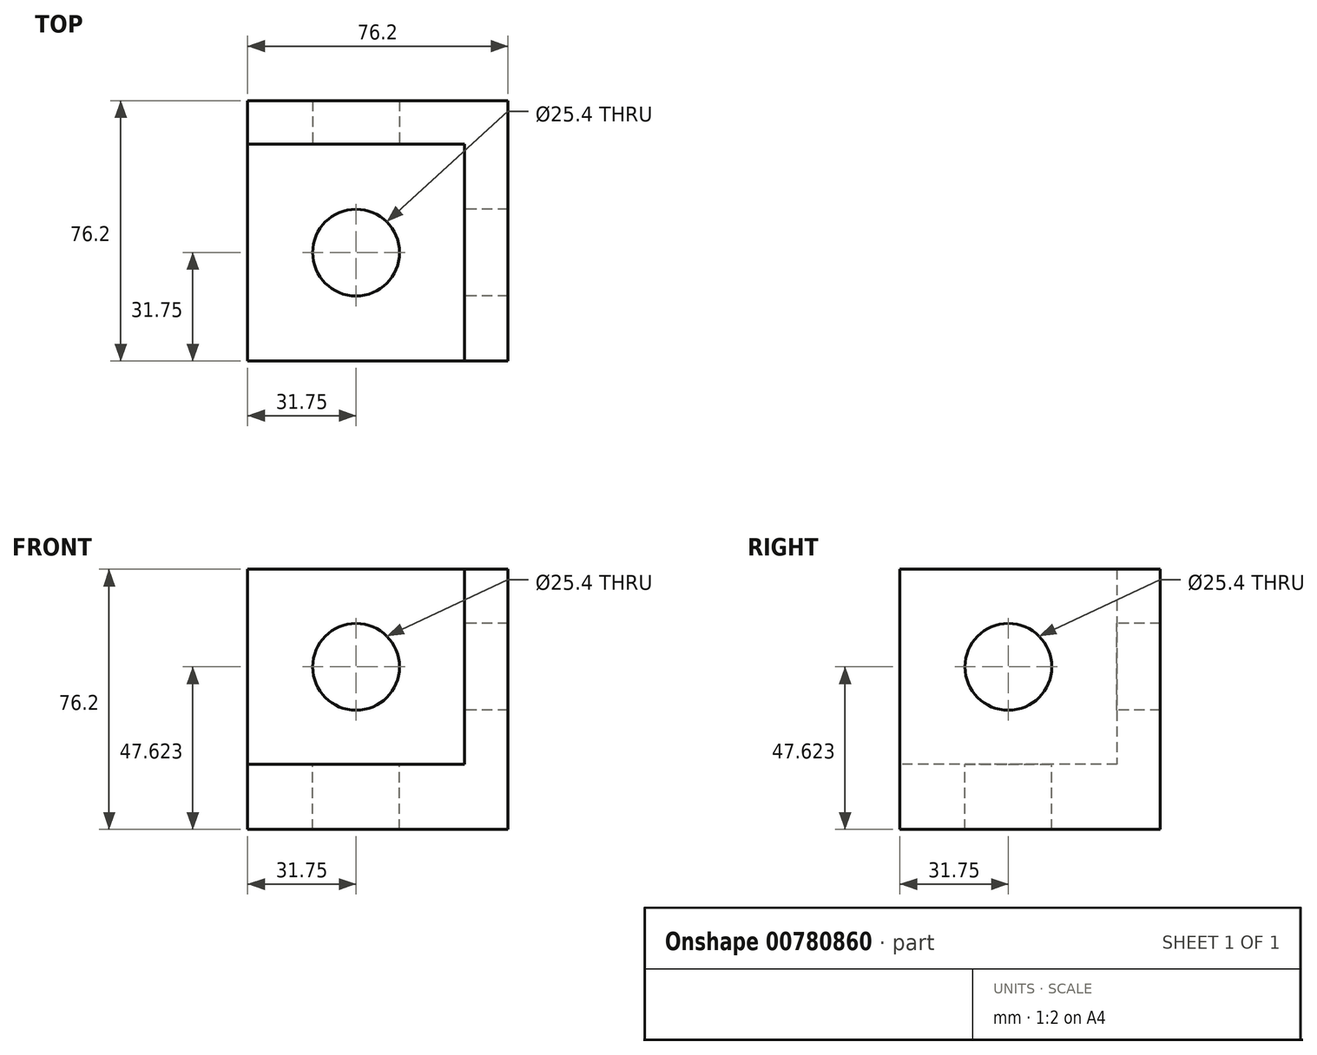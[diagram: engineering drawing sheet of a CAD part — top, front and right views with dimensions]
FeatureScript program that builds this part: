
annotation { "Feature Type Name" : "Feature", "Feature Type Description" : "" }
export const myFeature = defineFeature(function(context is Context, id is Id, definition is map)
    precondition{}
    {
        {
            var Q0;
            Q0=qCreatedBy(makeId("Front.planeOp"),FACE);
            var sketch = newSketch(context, id + "F0", { "sketchPlane" : qUnion([Q0])});
            skLineSegment(sketch, "E0", {"start": v(-44.12, -21.72) * mm, "end": v(32.08, -21.72) * mm});
            skLineSegment(sketch, "E1", {"start": v(32.08, -21.72) * mm, "end": v(32.08, 54.48) * mm});
            skLineSegment(sketch, "E2", {"start": v(32.08, 54.48) * mm, "end": v(-44.12, 54.48) * mm});
            skLineSegment(sketch, "E3", {"start": v(-44.12, 54.48) * mm, "end": v(-44.12, -21.72) * mm});
            skSolve(sketch);
        }
        {
            var Q0;
            Q0 = qSketchRegion(id + "F0", true);
            extrude(context, id + "F1", {"entities" : qUnion([Q0]), "depth" : 76.2 * mm, "offsetDistance" : 25.4 * mm});
        }
        {
            var Q0;
            Q0=makeQuery(id+"F1.opExtrude","CAP_FACE",FACE,{"disambiguationData":[OSD([sQuery(id+"F0.wireOp",EDGE,"E0"),sQuery(id+"F0.wireOp",EDGE,"E1"),sQuery(id+"F0.wireOp",EDGE,"E2"),sQuery(id+"F0.wireOp",EDGE,"E3")])],"isStart":false});
            var sketch = newSketch(context, id + "F2", { "sketchPlane" : qUnion([Q0])});
            skPoint(sketch, "E4.start.orphan", {"position": v(-44.12, 16.38) * mm});
            skLineSegment(sketch, "E5", {"start": v(-44.12, -2.67) * mm, "end": v(19.38, -2.67) * mm});
            skPoint(sketch, "E6.start.orphan", {"position": v(19.38, -21.72) * mm});
            skLineSegment(sketch, "E7", {"start": v(19.38, -2.67) * mm, "end": v(19.38, 54.48) * mm});
            skLineSegment(sketch, "E8", {"start": v(19.38, 54.48) * mm, "end": v(-44.12, 54.48) * mm});
            skLineSegment(sketch, "E9", {"start": v(-44.12, 54.48) * mm, "end": v(-44.12, -2.67) * mm});
            skSolve(sketch);
        }
        {
            var Q0;
            Q0 = qSketchRegion(id + "F2", true);
            extrude(context, id + "F3", {"entities" : qUnion([Q0]), "operationType" : NewBodyOperationType.REMOVE, "oppositeDirection" : true, "depth" : 63.5 * mm, "offsetDistance" : 25.4 * mm});
        }
        {
            var Q0;
            Q0=makeQuery(id+"F3.boolean.opBoolean","COPY",FACE,{"derivedFrom":makeQuery(id+"F3.opExtrude","SWEPT_FACE",FACE,{"disambiguationData":[OSD([sQuery(id+"F2.wireOp",EDGE,"E5")])]})});
            var sketch = newSketch(context, id + "F4", { "sketchPlane" : qUnion([Q0])});
            skLineSegment(sketch, "E10", {"start": v(-44.12, -76.2) * mm, "end": v(-12.37, -76.2) * mm});
            skCircle(sketch, "E11", {"center": v(-12.37, -44.45) * mm, "radius": 12.7 * mm});
            skPoint(sketch, "E12.end.orphan", {"position": v(-44.12, -44.45) * mm});
            skSolve(sketch);
        }
        {
            var Q0;
            Q0=makeQuery(id+"F3.boolean.opBoolean","COPY",FACE,{"derivedFrom":makeQuery(id+"F3.opExtrude","SWEPT_FACE",FACE,{"disambiguationData":[OSD([sQuery(id+"F2.wireOp",EDGE,"E7")])]})});
            var sketch = newSketch(context, id + "F5", { "sketchPlane" : qUnion([Q0])});
            skCircle(sketch, "E13", {"center": v(44.45, 25.9) * mm, "radius": 12.7 * mm});
            skPoint(sketch, "E14.start.orphan", {"position": v(76.2, 25.9) * mm});
            skSolve(sketch);
        }
        {
            var Q0;
            Q0=makeQuery(id+"F3.boolean.opBoolean","COPY",FACE,{"derivedFrom":makeQuery(id+"F3.opExtrude","CAP_FACE",FACE,{"disambiguationData":[OSD([sQuery(id+"F2.wireOp",EDGE,"E5"),sQuery(id+"F2.wireOp",EDGE,"E7"),sQuery(id+"F2.wireOp",EDGE,"E8"),sQuery(id+"F2.wireOp",EDGE,"E9")])],"isStart":false})});
            var sketch = newSketch(context, id + "F6", { "sketchPlane" : qUnion([Q0])});
            skCircle(sketch, "E15", {"center": v(-12.37, 25.9) * mm, "radius": 12.7 * mm});
            skPoint(sketch, "E16.start.orphan", {"position": v(-44.12, 25.9) * mm});
            skSolve(sketch);
        }
        {
            var Q0;
            Q0=makeQuery(id+"F5.imprint","IMPRINT",FACE,{"disambiguationData":[TD([[makeQuery(id+"F5.imprint","IMPRINT",EDGE,{"derivedFrom":sQuery(id+"F5.wireOp",EDGE,"E13")}),1.0]])]});
            extrude(context, id + "F7", {"entities" : qUnion([Q0]), "operationType" : NewBodyOperationType.REMOVE, "oppositeDirection" : true, "depth" : 25.4 * mm, "offsetDistance" : 25.4 * mm});
        }
        {
            var Q0;
            Q0=makeQuery(id+"F6.imprint","IMPRINT",FACE,{"disambiguationData":[TD([[makeQuery(id+"F6.imprint","IMPRINT",EDGE,{"derivedFrom":sQuery(id+"F6.wireOp",EDGE,"E15")}),1.0]])]});
            extrude(context, id + "F8", {"entities" : qUnion([Q0]), "operationType" : NewBodyOperationType.REMOVE, "oppositeDirection" : true, "depth" : 25.4 * mm, "offsetDistance" : 25.4 * mm});
        }
        {
            var Q0;
            Q0 = qSketchRegion(id + "F4", true);
            extrude(context, id + "F9", {"entities" : qUnion([Q0]), "operationType" : NewBodyOperationType.REMOVE, "oppositeDirection" : true, "depth" : 25.4 * mm, "offsetDistance" : 25.4 * mm});
        }
    });
